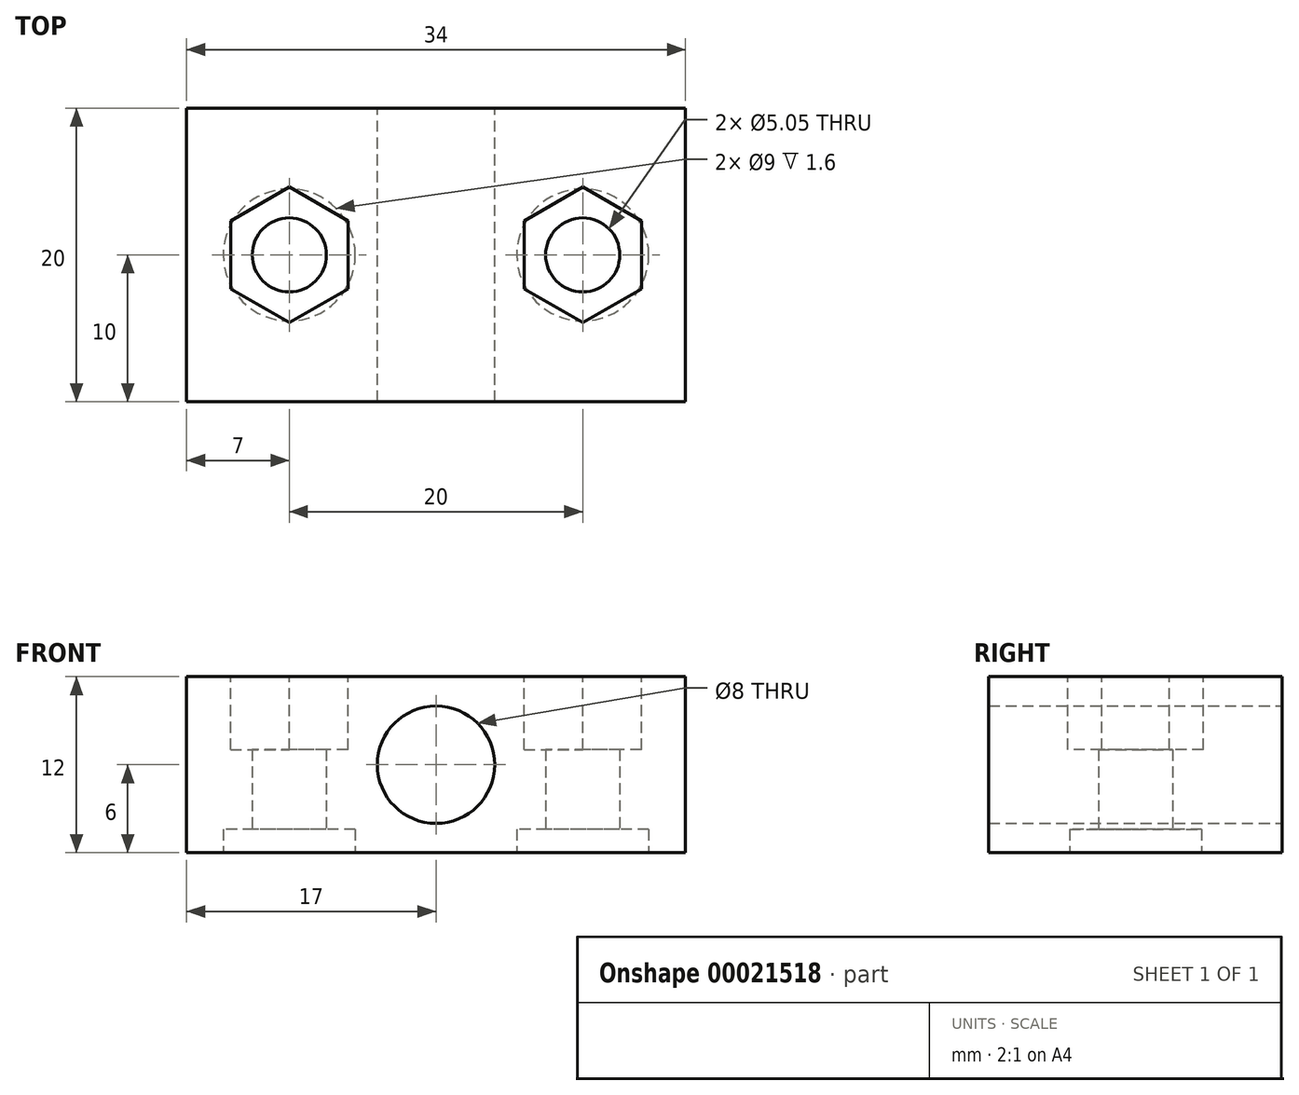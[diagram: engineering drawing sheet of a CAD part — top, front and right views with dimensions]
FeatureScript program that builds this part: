
annotation { "Feature Type Name" : "Feature", "Feature Type Description" : "" }
export const myFeature = defineFeature(function(context is Context, id is Id, definition is map)
    precondition{}
    {
        {
            var Q0;
            Q0=qCreatedBy(makeId("Top.planeOp"),FACE);
            var sketch = newSketch(context, id + "F0", { "sketchPlane" : qUnion([Q0])});
            skLineSegment(sketch, "E0.rect.bottom", {"start": v(17, 10) * mm, "end": v(-17, 10) * mm});
            skLineSegment(sketch, "E0.rect.top", {"start": v(17, -10) * mm, "end": v(-17, -10) * mm});
            skLineSegment(sketch, "E0.rect.left", {"start": v(17, 10) * mm, "end": v(17, -10) * mm});
            skLineSegment(sketch, "E0.rect.right", {"start": v(-17, 10) * mm, "end": v(-17, -10) * mm});
            skPoint(sketch, "E0.rect.middle", {"position": v(0, 0) * mm});
            skCircle(sketch, "E1", {"center": v(10, 0) * mm, "radius": 2.52 * mm});
            skCircle(sketch, "E2", {"center": v(10, 0) * mm, "radius": 4.5 * mm});
            skCircle(sketch, "E3", {"center": v(-10, 0) * mm, "radius": 2.52 * mm});
            skCircle(sketch, "E4", {"center": v(-10, 0) * mm, "radius": 4.5 * mm});
            skSolve(sketch);
        }
        {
            var Q0;
            Q0 = qSketchRegion(id + "F0", true);
            var Q1;
            Q1=makeQuery(id+"F0.imprint","IMPRINT",FACE,{"disambiguationData":[TD([[makeQuery(id+"F0.imprint","IMPRINT",EDGE,{"derivedFrom":sQuery(id+"F0.wireOp",EDGE,"E3")}),-1.0]])]});
            var Q2;
            Q2=makeQuery(id+"F0.imprint","IMPRINT",FACE,{"disambiguationData":[TD([[makeQuery(id+"F0.imprint","IMPRINT",EDGE,{"derivedFrom":sQuery(id+"F0.wireOp",EDGE,"E1")}),-1.0]])]});
            extrude(context, id + "F1", {"entities" : qUnion([Q0, Q1, Q2]), "depth" : 12 * mm});
        }
        {
            var Q0;
            Q0=makeQuery(id+"F0.imprint","IMPRINT",FACE,{"disambiguationData":[TD([[makeQuery(id+"F0.imprint","IMPRINT",EDGE,{"derivedFrom":sQuery(id+"F0.wireOp",EDGE,"E3")}),-1.0]])]});
            var Q1;
            Q1=makeQuery(id+"F0.imprint","IMPRINT",FACE,{"disambiguationData":[TD([[makeQuery(id+"F0.imprint","IMPRINT",EDGE,{"derivedFrom":sQuery(id+"F0.wireOp",EDGE,"E1")}),-1.0]])]});
            extrude(context, id + "F2", {"entities" : qUnion([Q0, Q1]), "operationType" : NewBodyOperationType.REMOVE, "depth" : 1.6 * mm});
        }
        {
            var Q0;
            Q0=makeQuery(id+"F1.opExtrude","CAP_FACE",FACE,{"disambiguationData":[OSD([sQuery(id+"F0.wireOp",EDGE,"E0.rect.bottom"),sQuery(id+"F0.wireOp",EDGE,"E0.rect.top"),sQuery(id+"F0.wireOp",EDGE,"E0.rect.left"),sQuery(id+"F0.wireOp",EDGE,"E0.rect.right"),sQuery(id+"F0.wireOp",EDGE,"E1"),sQuery(id+"F0.wireOp",EDGE,"E3")])],"isStart":false});
            var sketch = newSketch(context, id + "F3", { "sketchPlane" : qUnion([Q0])});
            skCircle(sketch, "E5.cCircle", {"center": v(-10, 0) * mm, "radius": 4 * mm, "construction": true});
            skLineSegment(sketch, "E5.0", {"start": v(-6, -2.31) * mm, "end": v(-10, -4.62) * mm});
            skLineSegment(sketch, "E5.1", {"start": v(-10, -4.62) * mm, "end": v(-14, -2.31) * mm});
            skLineSegment(sketch, "E5.2", {"start": v(-14, -2.31) * mm, "end": v(-14, 2.31) * mm});
            skLineSegment(sketch, "E5.3", {"start": v(-14, 2.3) * mm, "end": v(-10, 4.62) * mm});
            skLineSegment(sketch, "E5.4", {"start": v(-10, 4.62) * mm, "end": v(-6, 2.31) * mm});
            skLineSegment(sketch, "E5.5", {"start": v(-6, 2.3) * mm, "end": v(-6, -2.31) * mm});
            skPoint(sketch, "E5.0.midPoint", {"position": v(-8, -3.47) * mm});
            skCircle(sketch, "E6.cCircle", {"center": v(10, 0) * mm, "radius": 4 * mm, "construction": true});
            skLineSegment(sketch, "E6.0", {"start": v(14, -2.3) * mm, "end": v(10, -4.62) * mm});
            skLineSegment(sketch, "E6.1", {"start": v(10, -4.62) * mm, "end": v(6, -2.31) * mm});
            skLineSegment(sketch, "E6.2", {"start": v(6, -2.31) * mm, "end": v(6, 2.3) * mm});
            skLineSegment(sketch, "E6.3", {"start": v(6, 2.3) * mm, "end": v(10, 4.62) * mm});
            skLineSegment(sketch, "E6.4", {"start": v(10, 4.62) * mm, "end": v(14, 2.31) * mm});
            skLineSegment(sketch, "E6.5", {"start": v(14, 2.31) * mm, "end": v(14, -2.3) * mm});
            skPoint(sketch, "E6.0.midPoint", {"position": v(12, -3.47) * mm});
            skSolve(sketch);
        }
        {
            var Q0;
            Q0=makeQuery(id+"F3.imprint","IMPRINT",FACE,{"disambiguationData":[TD([[makeQuery(id+"F3.imprint","IMPRINT",EDGE,{"derivedFrom":sQuery(id+"F3.wireOp",EDGE,"E6.0")}),-1.0]])]});
            var Q1;
            Q1=makeQuery(id+"F3.imprint","IMPRINT",FACE,{"disambiguationData":[TD([[makeQuery(id+"F3.imprint","IMPRINT",EDGE,{"derivedFrom":sQuery(id+"F3.wireOp",EDGE,"E5.0")}),-1.0]])]});
            extrude(context, id + "F4", {"entities" : qUnion([Q0, Q1]), "operationType" : NewBodyOperationType.REMOVE, "oppositeDirection" : true, "depth" : 4.97 * mm});
        }
        {
            var Q0;
            Q0=makeQuery(id+"F1.opExtrude","SWEPT_FACE",FACE,{"disambiguationData":[OSD([sQuery(id+"F0.wireOp",EDGE,"E0.rect.bottom")])]});
            var sketch = newSketch(context, id + "F5", { "sketchPlane" : qUnion([Q0])});
            skCircle(sketch, "E7", {"center": v(0, 6) * mm, "radius": 4 * mm});
            skSolve(sketch);
        }
        {
            var Q0;
            Q0=makeQuery(id+"F5.imprint","IMPRINT",FACE,{"disambiguationData":[TD([[makeQuery(id+"F5.imprint","IMPRINT",EDGE,{"derivedFrom":sQuery(id+"F5.wireOp",EDGE,"E7")}),1.0]])]});
            extrude(context, id + "F6", {"entities" : qUnion([Q0]), "operationType" : NewBodyOperationType.REMOVE, "oppositeDirection" : true, "depth" : 20 * mm});
        }
    });
